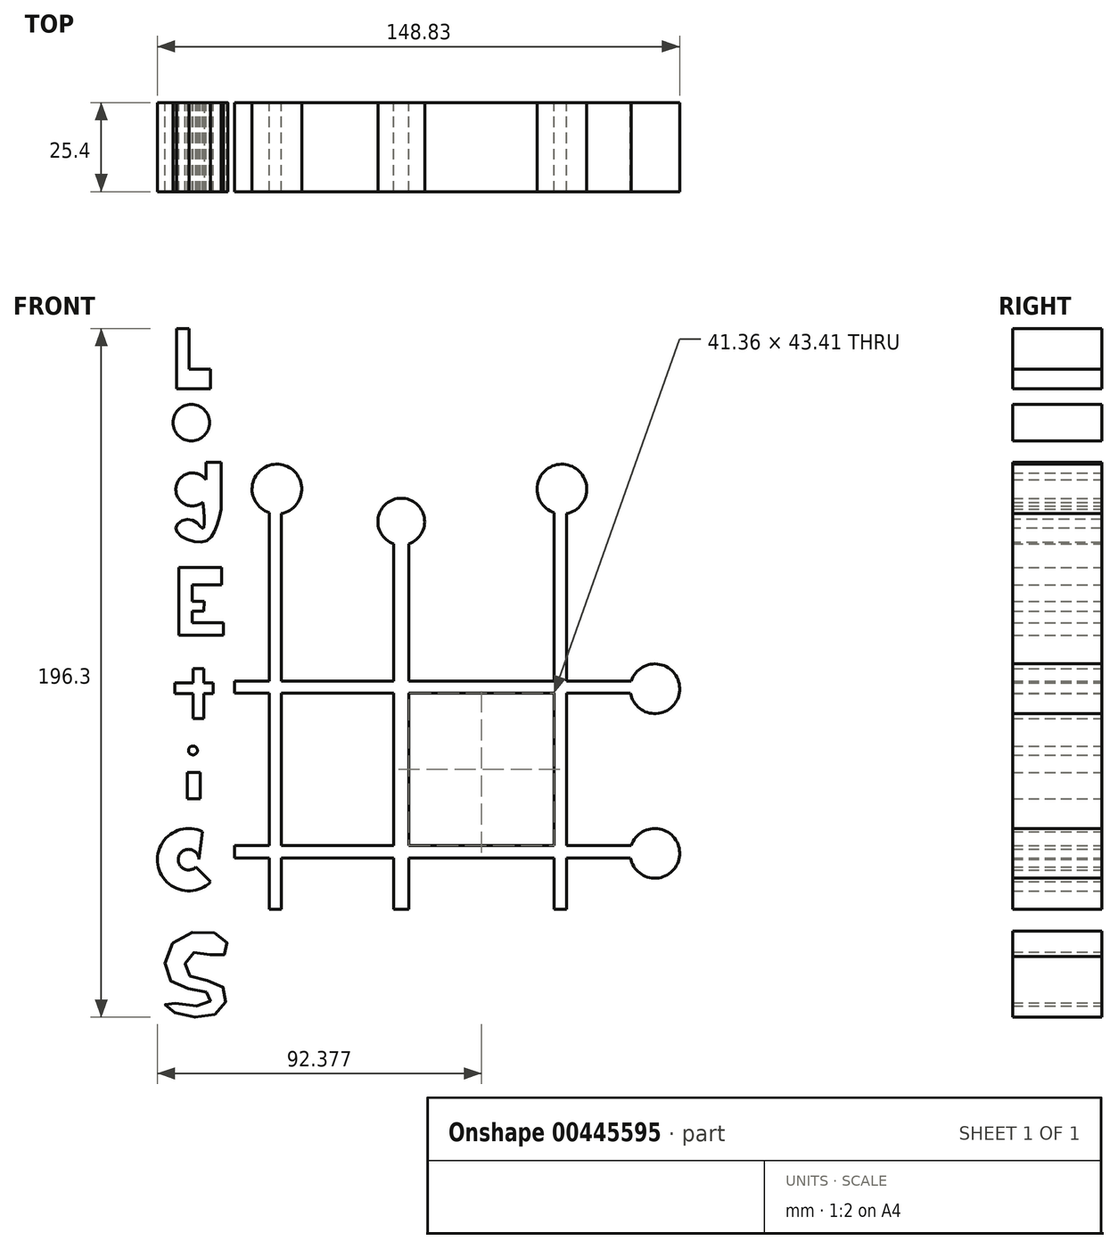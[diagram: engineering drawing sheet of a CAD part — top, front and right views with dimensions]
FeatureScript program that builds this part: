
annotation { "Feature Type Name" : "Feature", "Feature Type Description" : "" }
export const myFeature = defineFeature(function(context is Context, id is Id, definition is map)
    precondition{}
    {
        {
            var Q0;
            Q0=qCreatedBy(makeId("Front.planeOp"),FACE);
            var sketch = newSketch(context, id + "F0", { "sketchPlane" : qUnion([Q0])});
            skLineSegment(sketch, "E0", {"start": v(-57.22, -42.33) * mm, "end": v(55.59, -42.33) * mm});
            skLineSegment(sketch, "E1", {"start": v(-57.22, -38.84) * mm, "end": v(55.82, -38.84) * mm});
            skArc(sketch, "E2", {"start": v(55.59, -42.33) * mm, "mid": v(69.6, -41.51) * mm, "end": v(55.82, -38.84) * mm});
            skLineSegment(sketch, "E3", {"start": v(-57.22, 4.57) * mm, "end": v(55.59, 4.57) * mm});
            skLineSegment(sketch, "E4", {"start": v(-57.22, 8.06) * mm, "end": v(55.82, 8.06) * mm});
            skArc(sketch, "E5", {"start": v(55.59, 4.57) * mm, "mid": v(69.6, 5.39) * mm, "end": v(55.82, 8.06) * mm});
            skLineSegment(sketch, "E6", {"start": v(-43.88, -56.98) * mm, "end": v(-43.88, 55.82) * mm});
            skLineSegment(sketch, "E7", {"start": v(-47.37, -56.98) * mm, "end": v(-47.37, 56.05) * mm});
            skArc(sketch, "E8", {"start": v(-43.88, 55.82) * mm, "mid": v(-44.7, 69.84) * mm, "end": v(-47.37, 56.05) * mm});
            skLineSegment(sketch, "E9", {"start": v(37.34, -56.98) * mm, "end": v(37.34, 55.82) * mm});
            skLineSegment(sketch, "E10", {"start": v(33.85, -56.98) * mm, "end": v(33.85, 56.05) * mm});
            skArc(sketch, "E11", {"start": v(37.34, 55.82) * mm, "mid": v(36.52, 69.84) * mm, "end": v(33.85, 56.05) * mm});
            skLineSegment(sketch, "E12", {"start": v(-11.93, -56.98) * mm, "end": v(-11.93, 47.22) * mm});
            skArc(sketch, "E13", {"start": v(-7.51, 47.22) * mm, "mid": v(-9.72, 60.17) * mm, "end": v(-11.93, 47.22) * mm});
            skLineSegment(sketch, "E14", {"start": v(-7.51, 47.22) * mm, "end": v(-7.51, -56.98) * mm});
            skLineSegment(sketch, "E15", {"start": v(-57.22, 8.06) * mm, "end": v(-57.22, 4.57) * mm});
            skLineSegment(sketch, "E16", {"start": v(-57.22, -38.84) * mm, "end": v(-57.22, -42.33) * mm});
            skLineSegment(sketch, "E17", {"start": v(-47.37, -56.98) * mm, "end": v(-43.88, -56.98) * mm});
            skLineSegment(sketch, "E18", {"start": v(-11.93, -56.98) * mm, "end": v(-7.51, -56.98) * mm});
            skLineSegment(sketch, "E19", {"start": v(33.85, -56.98) * mm, "end": v(37.34, -56.98) * mm});
            skLineSegment(sketch, "E20", {"start": v(-73.71, 91.4) * mm, "end": v(-64.03, 91.4) * mm});
            skLineSegment(sketch, "E21", {"start": v(-64.03, 91.4) * mm, "end": v(-64.03, 96.93) * mm});
            skLineSegment(sketch, "E22", {"start": v(-64.03, 96.93) * mm, "end": v(-70.11, 96.93) * mm});
            skLineSegment(sketch, "E23", {"start": v(-70.11, 96.93) * mm, "end": v(-70.11, 108.54) * mm});
            skLineSegment(sketch, "E24", {"start": v(-73.71, 91.4) * mm, "end": v(-73.71, 108.54) * mm});
            skLineSegment(sketch, "E25", {"start": v(-73.71, 108.54) * mm, "end": v(-70.11, 108.54) * mm});
            skCircle(sketch, "E26", {"center": v(-69.56, 81.71) * mm, "radius": 5.2 * mm});
            skArc(sketch, "E27", {"start": v(-65.41, 65.4) * mm, "mid": v(-73.9, 63.27) * mm, "end": v(-66.24, 59.03) * mm});
            skLineSegment(sketch, "E28", {"start": v(-65.41, 65.4) * mm, "end": v(-65.41, 70.37) * mm});
            skLineSegment(sketch, "E29", {"start": v(-60.99, 70.37) * mm, "end": v(-65.41, 70.37) * mm});
            skLineSegment(sketch, "E30", {"start": v(-60.99, 70.37) * mm, "end": v(-60.99, 57.1) * mm});
            skFitSpline(sketch, "E31", {"points": [v(-60.99, 57.1) * mm, v(-66.24, 47.7) * mm, v(-73.99, 51.55) * mm, v(-69.56, 54.05) * mm, v(-66.24, 51.55) * mm, v(-66.24, 59.03) * mm], "startDerivative": vector(-12.14, -52.91) * mm, "endDerivative": vector(-5.05, 54.28) * mm});
            skLineSegment(sketch, "E32", {"start": v(-73.16, 21.14) * mm, "end": v(-60.43, 21.14) * mm});
            skLineSegment(sketch, "E33", {"start": v(-60.43, 21.14) * mm, "end": v(-60.43, 24.74) * mm});
            skLineSegment(sketch, "E34", {"start": v(-60.43, 24.74) * mm, "end": v(-69.28, 24.74) * mm});
            skLineSegment(sketch, "E35", {"start": v(-73.16, 21.14) * mm, "end": v(-73.16, 40.38) * mm});
            skLineSegment(sketch, "E36", {"start": v(-60.94, 40.38) * mm, "end": v(-73.16, 40.38) * mm});
            skLineSegment(sketch, "E37", {"start": v(-60.94, 40.38) * mm, "end": v(-60.94, 35.5) * mm});
            skLineSegment(sketch, "E38", {"start": v(-60.94, 35.5) * mm, "end": v(-69.28, 35.5) * mm});
            skLineSegment(sketch, "E39", {"start": v(-69.28, 35.5) * mm, "end": v(-69.28, 30.76) * mm});
            skPoint(sketch, "E39.endSnap0", {"position": v(-73.16, 30.76) * mm});
            skLineSegment(sketch, "E40", {"start": v(-69.28, 30.76) * mm, "end": v(-65.9, 30.76) * mm});
            skLineSegment(sketch, "E41", {"start": v(-65.9, 30.76) * mm, "end": v(-66.01, 28) * mm});
            skLineSegment(sketch, "E42", {"start": v(-66.01, 28) * mm, "end": v(-69.28, 28) * mm});
            skLineSegment(sketch, "E43", {"start": v(-69.28, 28) * mm, "end": v(-69.28, 24.74) * mm});
            skLineSegment(sketch, "E44.bottom", {"start": v(-69.08, 11.54) * mm, "end": v(-66.05, 11.54) * mm});
            skLineSegment(sketch, "E44.top", {"start": v(-69.08, -2.65) * mm, "end": v(-66.05, -2.65) * mm});
            skLineSegment(sketch, "E44.left", {"start": v(-69.08, 11.54) * mm, "end": v(-69.08, -2.65) * mm});
            skLineSegment(sketch, "E44.right", {"start": v(-66.05, 11.54) * mm, "end": v(-66.05, -2.65) * mm});
            skPoint(sketch, "E45.oppositeSnap0", {"position": v(-66.05, 4.45) * mm});
            skLineSegment(sketch, "E45.bottom", {"start": v(-74.2, 7.59) * mm, "end": v(-63.26, 7.59) * mm});
            skLineSegment(sketch, "E45.top", {"start": v(-74.2, 4.45) * mm, "end": v(-63.26, 4.45) * mm});
            skLineSegment(sketch, "E45.left", {"start": v(-74.2, 7.59) * mm, "end": v(-74.2, 4.45) * mm});
            skLineSegment(sketch, "E45.right", {"start": v(-63.26, 7.59) * mm, "end": v(-63.26, 4.45) * mm});
            skLineSegment(sketch, "E46.bottom", {"start": v(-70.64, -18) * mm, "end": v(-66.99, -18) * mm});
            skLineSegment(sketch, "E46.top", {"start": v(-70.64, -25.44) * mm, "end": v(-66.99, -25.44) * mm});
            skLineSegment(sketch, "E46.left", {"start": v(-66.99, -18) * mm, "end": v(-66.99, -25.44) * mm});
            skLineSegment(sketch, "E46.right", {"start": v(-70.64, -18) * mm, "end": v(-70.64, -25.44) * mm});
            skPoint(sketch, "E47.centerSnap0", {"position": v(-66.99, -21.72) * mm});
            skCircle(sketch, "E48", {"center": v(-69.08, -11.72) * mm, "radius": 1.28 * mm});
            skPoint(sketch, "E48.centerSnap0", {"position": v(-69.08, 4.45) * mm});
            skArc(sketch, "E49", {"start": v(-66.33, -34.9) * mm, "mid": v(-79.1, -44.26) * mm, "end": v(-64.03, -49.13) * mm});
            skLineSegment(sketch, "E50", {"start": v(-64.03, -49.13) * mm, "end": v(-68.23, -44.92) * mm});
            skLineSegment(sketch, "E51", {"start": v(-66.33, -34.9) * mm, "end": v(-67.37, -42.73) * mm});
            skArc(sketch, "E52", {"start": v(-67.37, -42.73) * mm, "mid": v(-73.06, -41.76) * mm, "end": v(-68.23, -44.92) * mm});
            skFitSpline(sketch, "E53", {"points": [v(-74.2, -86.39) * mm, v(-61.23, -85.86) * mm, v(-60.97, -78.72) * mm, v(-70.76, -75.28) * mm, v(-69.17, -69.46) * mm, v(-60.7, -70.25) * mm, v(-59.9, -65.49) * mm, v(-73.67, -65.49) * mm, v(-75.25, -77.66) * mm, v(-64.4, -81.1) * mm, v(-65.46, -84.27) * mm, v(-76.84, -83.74) * mm, v(-74.2, -86.39) * mm]});
            skSolve(sketch);
        }
        {
            var Q0;
            {var subQ0=sQuery(id+"F0.wireOp",EDGE,"E15");Q0=makeQuery(id+"F0.imprint","IMPRINT",FACE,{"disambiguationData":[TD([[makeQuery(id+"F0.imprint","IMPRINT",EDGE,{"derivedFrom":subQ0}),1.0]])]});}
            var Q1;
            {var subQ0=sQuery(id+"F0.wireOp",EDGE,"E16");Q1=makeQuery(id+"F0.imprint","IMPRINT",FACE,{"disambiguationData":[TD([[makeQuery(id+"F0.imprint","IMPRINT",EDGE,{"derivedFrom":subQ0}),1.0]])]});}
            var Q2;
            {var subQ0=sQuery(id+"F0.wireOp",EDGE,"E6");var subQ1=sQuery(id+"F0.wireOp",EDGE,"E0");var subQ2=makeQuery(id+"F0.imprint","INTERSECT",VERTEX,{"derivedFrom":[subQ1,subQ0]});Q2=makeQuery(id+"F0.imprint","IMPRINT",FACE,{"disambiguationData":[TD([[makeQuery(id+"F0.imprint","IMPRINT",EDGE,{"disambiguationData":[TD([[subQ2,-1.0]])],"derivedFrom":subQ1}),1.0]])]});}
            var Q3;
            {var subQ0=sQuery(id+"F0.wireOp",EDGE,"E7");var subQ1=sQuery(id+"F0.wireOp",EDGE,"E0");var subQ2=makeQuery(id+"F0.imprint","INTERSECT",VERTEX,{"derivedFrom":[subQ1,subQ0]});Q3=makeQuery(id+"F0.imprint","IMPRINT",FACE,{"disambiguationData":[TD([[makeQuery(id+"F0.imprint","IMPRINT",EDGE,{"disambiguationData":[TD([[subQ2,-1.0]])],"derivedFrom":subQ1}),1.0]])]});}
            var Q4;
            {var subQ5=sQuery(id+"F0.wireOp",EDGE,"E17");Q4=makeQuery(id+"F0.imprint","IMPRINT",FACE,{"disambiguationData":[TD([[makeQuery(id+"F0.imprint","IMPRINT",EDGE,{"derivedFrom":subQ5}),1.0]])]});}
            var Q5;
            {var subQ0=sQuery(id+"F0.wireOp",EDGE,"E7");var subQ1=sQuery(id+"F0.wireOp",EDGE,"E1");var subQ2=makeQuery(id+"F0.imprint","INTERSECT",VERTEX,{"derivedFrom":[subQ1,subQ0]});Q5=makeQuery(id+"F0.imprint","IMPRINT",FACE,{"disambiguationData":[TD([[makeQuery(id+"F0.imprint","IMPRINT",EDGE,{"disambiguationData":[TD([[subQ2,-1.0]])],"derivedFrom":subQ1}),1.0]])]});}
            var Q6;
            {var subQ0=sQuery(id+"F0.wireOp",EDGE,"E7");var subQ1=sQuery(id+"F0.wireOp",EDGE,"E3");var subQ2=makeQuery(id+"F0.imprint","INTERSECT",VERTEX,{"derivedFrom":[subQ1,subQ0]});Q6=makeQuery(id+"F0.imprint","IMPRINT",FACE,{"disambiguationData":[TD([[makeQuery(id+"F0.imprint","IMPRINT",EDGE,{"disambiguationData":[TD([[subQ2,-1.0]])],"derivedFrom":subQ1}),1.0]])]});}
            var Q7;
            {var subQ5=sQuery(id+"F0.wireOp",EDGE,"E8");Q7=makeQuery(id+"F0.imprint","IMPRINT",FACE,{"disambiguationData":[TD([[makeQuery(id+"F0.imprint","IMPRINT",EDGE,{"derivedFrom":subQ5}),1.0]])]});}
            var Q8;
            {var subQ0=sQuery(id+"F0.wireOp",EDGE,"E6");var subQ1=sQuery(id+"F0.wireOp",EDGE,"E3");var subQ2=makeQuery(id+"F0.imprint","INTERSECT",VERTEX,{"derivedFrom":[subQ1,subQ0]});Q8=makeQuery(id+"F0.imprint","IMPRINT",FACE,{"disambiguationData":[TD([[makeQuery(id+"F0.imprint","IMPRINT",EDGE,{"disambiguationData":[TD([[subQ2,-1.0]])],"derivedFrom":subQ1}),1.0]])]});}
            var Q9;
            {var subQ5=sQuery(id+"F0.wireOp",EDGE,"E13");Q9=makeQuery(id+"F0.imprint","IMPRINT",FACE,{"disambiguationData":[TD([[makeQuery(id+"F0.imprint","IMPRINT",EDGE,{"derivedFrom":subQ5}),1.0]])]});}
            var Q10;
            {var subQ0=sQuery(id+"F0.wireOp",EDGE,"E12");var subQ1=sQuery(id+"F0.wireOp",EDGE,"E3");var subQ2=makeQuery(id+"F0.imprint","INTERSECT",VERTEX,{"derivedFrom":[subQ1,subQ0]});Q10=makeQuery(id+"F0.imprint","IMPRINT",FACE,{"disambiguationData":[TD([[makeQuery(id+"F0.imprint","IMPRINT",EDGE,{"disambiguationData":[TD([[subQ2,-1.0]])],"derivedFrom":subQ1}),1.0]])]});}
            var Q11;
            {var subQ0=sQuery(id+"F0.wireOp",EDGE,"E12");var subQ1=sQuery(id+"F0.wireOp",EDGE,"E1");var subQ2=makeQuery(id+"F0.imprint","INTERSECT",VERTEX,{"derivedFrom":[subQ1,subQ0]});Q11=makeQuery(id+"F0.imprint","IMPRINT",FACE,{"disambiguationData":[TD([[makeQuery(id+"F0.imprint","IMPRINT",EDGE,{"disambiguationData":[TD([[subQ2,-1.0]])],"derivedFrom":subQ1}),1.0]])]});}
            var Q12;
            {var subQ5=sQuery(id+"F0.wireOp",EDGE,"E18");Q12=makeQuery(id+"F0.imprint","IMPRINT",FACE,{"disambiguationData":[TD([[makeQuery(id+"F0.imprint","IMPRINT",EDGE,{"derivedFrom":subQ5}),1.0]])]});}
            var Q13;
            {var subQ0=sQuery(id+"F0.wireOp",EDGE,"E12");var subQ1=sQuery(id+"F0.wireOp",EDGE,"E0");var subQ2=makeQuery(id+"F0.imprint","INTERSECT",VERTEX,{"derivedFrom":[subQ1,subQ0]});Q13=makeQuery(id+"F0.imprint","IMPRINT",FACE,{"disambiguationData":[TD([[makeQuery(id+"F0.imprint","IMPRINT",EDGE,{"disambiguationData":[TD([[subQ2,-1.0]])],"derivedFrom":subQ1}),1.0]])]});}
            var Q14;
            {var subQ0=sQuery(id+"F0.wireOp",EDGE,"E14");var subQ1=sQuery(id+"F0.wireOp",EDGE,"E0");var subQ2=makeQuery(id+"F0.imprint","INTERSECT",VERTEX,{"derivedFrom":[subQ1,subQ0]});Q14=makeQuery(id+"F0.imprint","IMPRINT",FACE,{"disambiguationData":[TD([[makeQuery(id+"F0.imprint","IMPRINT",EDGE,{"disambiguationData":[TD([[subQ2,-1.0]])],"derivedFrom":subQ1}),1.0]])]});}
            var Q15;
            {var subQ5=sQuery(id+"F0.wireOp",EDGE,"E19");Q15=makeQuery(id+"F0.imprint","IMPRINT",FACE,{"disambiguationData":[TD([[makeQuery(id+"F0.imprint","IMPRINT",EDGE,{"derivedFrom":subQ5}),1.0]])]});}
            var Q16;
            {var subQ0=sQuery(id+"F0.wireOp",EDGE,"E10");var subQ1=sQuery(id+"F0.wireOp",EDGE,"E0");var subQ2=makeQuery(id+"F0.imprint","INTERSECT",VERTEX,{"derivedFrom":[subQ1,subQ0]});Q16=makeQuery(id+"F0.imprint","IMPRINT",FACE,{"disambiguationData":[TD([[makeQuery(id+"F0.imprint","IMPRINT",EDGE,{"disambiguationData":[TD([[subQ2,-1.0]])],"derivedFrom":subQ1}),1.0]])]});}
            var Q17;
            {var subQ0=sQuery(id+"F0.wireOp",EDGE,"E2");Q17=makeQuery(id+"F0.imprint","IMPRINT",FACE,{"disambiguationData":[TD([[makeQuery(id+"F0.imprint","IMPRINT",EDGE,{"derivedFrom":subQ0}),1.0]])]});}
            var Q18;
            {var subQ0=sQuery(id+"F0.wireOp",EDGE,"E9");var subQ1=sQuery(id+"F0.wireOp",EDGE,"E1");var subQ2=makeQuery(id+"F0.imprint","INTERSECT",VERTEX,{"derivedFrom":[subQ1,subQ0]});Q18=makeQuery(id+"F0.imprint","IMPRINT",FACE,{"disambiguationData":[TD([[makeQuery(id+"F0.imprint","IMPRINT",EDGE,{"disambiguationData":[TD([[subQ2,1.0]])],"derivedFrom":subQ1}),1.0]])]});}
            var Q19;
            {var subQ0=sQuery(id+"F0.wireOp",EDGE,"E5");Q19=makeQuery(id+"F0.imprint","IMPRINT",FACE,{"disambiguationData":[TD([[makeQuery(id+"F0.imprint","IMPRINT",EDGE,{"derivedFrom":subQ0}),1.0]])]});}
            var Q20;
            {var subQ5=sQuery(id+"F0.wireOp",EDGE,"E11");Q20=makeQuery(id+"F0.imprint","IMPRINT",FACE,{"disambiguationData":[TD([[makeQuery(id+"F0.imprint","IMPRINT",EDGE,{"derivedFrom":subQ5}),1.0]])]});}
            var Q21;
            {var subQ0=sQuery(id+"F0.wireOp",EDGE,"E14");var subQ1=sQuery(id+"F0.wireOp",EDGE,"E3");var subQ2=makeQuery(id+"F0.imprint","INTERSECT",VERTEX,{"derivedFrom":[subQ1,subQ0]});Q21=makeQuery(id+"F0.imprint","IMPRINT",FACE,{"disambiguationData":[TD([[makeQuery(id+"F0.imprint","IMPRINT",EDGE,{"disambiguationData":[TD([[subQ2,-1.0]])],"derivedFrom":subQ1}),1.0]])]});}
            var Q22;
            {var subQ0=sQuery(id+"F0.wireOp",EDGE,"E9");var subQ1=sQuery(id+"F0.wireOp",EDGE,"E3");var subQ2=makeQuery(id+"F0.imprint","INTERSECT",VERTEX,{"derivedFrom":[subQ1,subQ0]});Q22=makeQuery(id+"F0.imprint","IMPRINT",FACE,{"disambiguationData":[TD([[makeQuery(id+"F0.imprint","IMPRINT",EDGE,{"disambiguationData":[TD([[subQ2,1.0]])],"derivedFrom":subQ1}),1.0]])]});}
            extrude(context, id + "F1", {"entities" : qUnion([Q0, Q1, Q2, Q3, Q4, Q5, Q6, Q7, Q8, Q9, Q10, Q11, Q12, Q13, Q14, Q15, Q16, Q17, Q18, Q19, Q20, Q21, Q22]), "depth" : 25.4 * mm});
        }
        {
            var Q0;
            {var subQ5=sQuery(id+"F0.wireOp",EDGE,"E45.left");Q0=makeQuery(id+"F0.imprint","IMPRINT",FACE,{"disambiguationData":[TD([[makeQuery(id+"F0.imprint","IMPRINT",EDGE,{"derivedFrom":subQ5}),1.0]])]});}
            var Q1;
            {var subQ0=sQuery(id+"F0.wireOp",EDGE,"E44.top");Q1=makeQuery(id+"F0.imprint","IMPRINT",FACE,{"disambiguationData":[TD([[makeQuery(id+"F0.imprint","IMPRINT",EDGE,{"derivedFrom":subQ0}),1.0]])]});}
            var Q2;
            Q2=makeQuery(id+"F0.imprint","IMPRINT",FACE,{"disambiguationData":[TD([[makeQuery(id+"F0.imprint","IMPRINT",EDGE,{"derivedFrom":sQuery(id+"F0.wireOp",EDGE,"E20")}),1.0]])]});
            var Q3;
            Q3=makeQuery(id+"F0.imprint","IMPRINT",FACE,{"disambiguationData":[TD([[makeQuery(id+"F0.imprint","IMPRINT",EDGE,{"derivedFrom":sQuery(id+"F0.wireOp",EDGE,"E26")}),1.0]])]});
            var Q4;
            Q4=makeQuery(id+"F0.imprint","IMPRINT",FACE,{"disambiguationData":[TD([[makeQuery(id+"F0.imprint","IMPRINT",EDGE,{"derivedFrom":sQuery(id+"F0.wireOp",EDGE,"E27")}),1.0]])]});
            var Q5;
            Q5=makeQuery(id+"F0.imprint","IMPRINT",FACE,{"disambiguationData":[TD([[makeQuery(id+"F0.imprint","IMPRINT",EDGE,{"derivedFrom":sQuery(id+"F0.wireOp",EDGE,"E32")}),1.0]])]});
            var Q6;
            Q6=makeQuery(id+"F0.imprint","IMPRINT",FACE,{"disambiguationData":[TD([[makeQuery(id+"F0.imprint","IMPRINT",EDGE,{"derivedFrom":sQuery(id+"F0.wireOp",EDGE,"E46.bottom")}),-1.0]])]});
            var Q7;
            Q7=makeQuery(id+"F0.imprint","IMPRINT",FACE,{"disambiguationData":[TD([[makeQuery(id+"F0.imprint","IMPRINT",EDGE,{"derivedFrom":sQuery(id+"F0.wireOp",EDGE,"E49")}),1.0]])]});
            var Q8;
            Q8=makeQuery(id+"F0.imprint","IMPRINT",FACE,{"disambiguationData":[TD([[makeQuery(id+"F0.imprint","IMPRINT",EDGE,{"derivedFrom":sQuery(id+"F0.wireOp",EDGE,"E53")}),1.0]])]});
            var Q9;
            {var subQ0=sQuery(id+"F0.wireOp",EDGE,"E44.bottom");Q9=makeQuery(id+"F0.imprint","IMPRINT",FACE,{"disambiguationData":[TD([[makeQuery(id+"F0.imprint","IMPRINT",EDGE,{"derivedFrom":subQ0}),-1.0]])]});}
            var Q10;
            {var subQ0=sQuery(id+"F0.wireOp",EDGE,"E45.bottom");var subQ1=sQuery(id+"F0.wireOp",EDGE,"E44.left");var subQ2=makeQuery(id+"F0.imprint","INTERSECT",VERTEX,{"derivedFrom":[subQ1,subQ0]});Q10=makeQuery(id+"F0.imprint","IMPRINT",FACE,{"disambiguationData":[TD([[makeQuery(id+"F0.imprint","IMPRINT",EDGE,{"disambiguationData":[TD([[subQ2,-1.0]])],"derivedFrom":subQ1}),1.0]])]});}
            var Q11;
            {var subQ5=sQuery(id+"F0.wireOp",EDGE,"E45.right");Q11=makeQuery(id+"F0.imprint","IMPRINT",FACE,{"disambiguationData":[TD([[makeQuery(id+"F0.imprint","IMPRINT",EDGE,{"derivedFrom":subQ5}),-1.0]])]});}
            var Q12;
            Q12=makeQuery(id+"F0.imprint","IMPRINT",FACE,{"disambiguationData":[TD([[makeQuery(id+"F0.imprint","IMPRINT",EDGE,{"derivedFrom":sQuery(id+"F0.wireOp",EDGE,"E48")}),1.0]])]});
            extrude(context, id + "F2", {"entities" : qUnion([Q0, Q1, Q2, Q3, Q4, Q5, Q6, Q7, Q8, Q9, Q10, Q11, Q12]), "depth" : 25.4 * mm});
        }
    });
